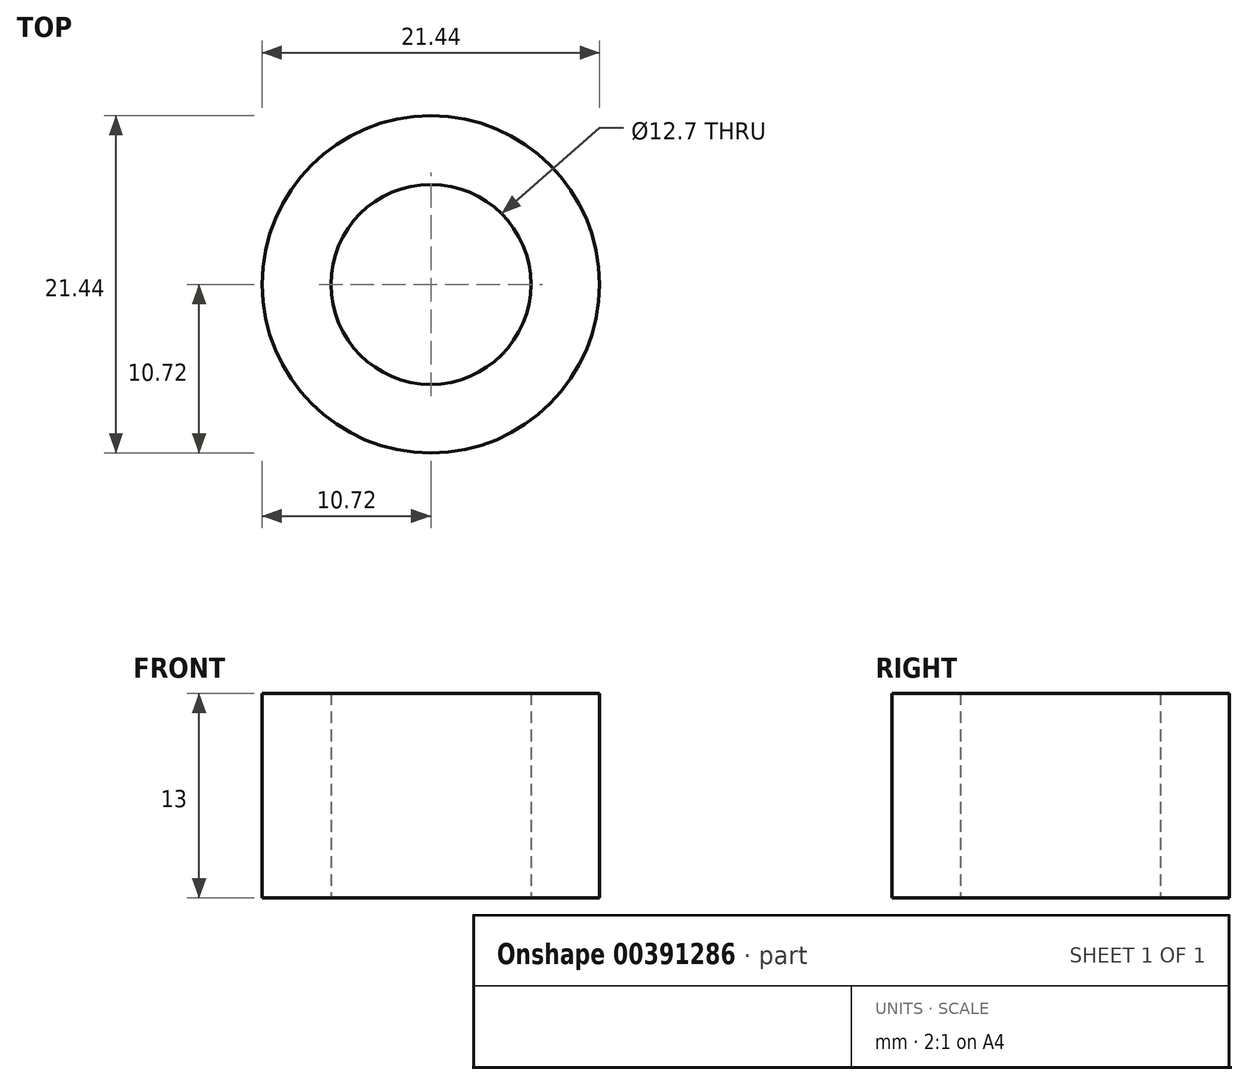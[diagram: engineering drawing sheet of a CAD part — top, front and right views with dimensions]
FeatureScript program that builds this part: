
annotation { "Feature Type Name" : "Feature", "Feature Type Description" : "" }
export const myFeature = defineFeature(function(context is Context, id is Id, definition is map)
    precondition{}
    {
        {
            assignVariable(context, id + "F0", {"name" : "Length", "anyValue" : 13});
        }
        {
            var Q0;
            Q0=qCreatedBy(makeId("Top.planeOp"),FACE);
            var sketch = newSketch(context, id + "F1", { "sketchPlane" : qUnion([Q0])});
            skCircle(sketch, "E0", {"center": v(0, 0) * mm, "radius": 10.72 * mm});
            skCircle(sketch, "E1", {"center": v(0, 0) * mm, "radius": 6.35 * mm});
            skSolve(sketch);
        }
        {
            var Q0;
            Q0=makeQuery(id+"F1.imprint","IMPRINT",FACE,{"disambiguationData":[TD([[makeQuery(id+"F1.imprint","IMPRINT",EDGE,{"derivedFrom":sQuery(id+"F1.wireOp",EDGE,"E0")}),1.0]])]});
            extrude(context, id + "F2", {"entities" : qUnion([Q0]), "depth" : (getVariable(context, 'Length')) * mm});
        }
    });
